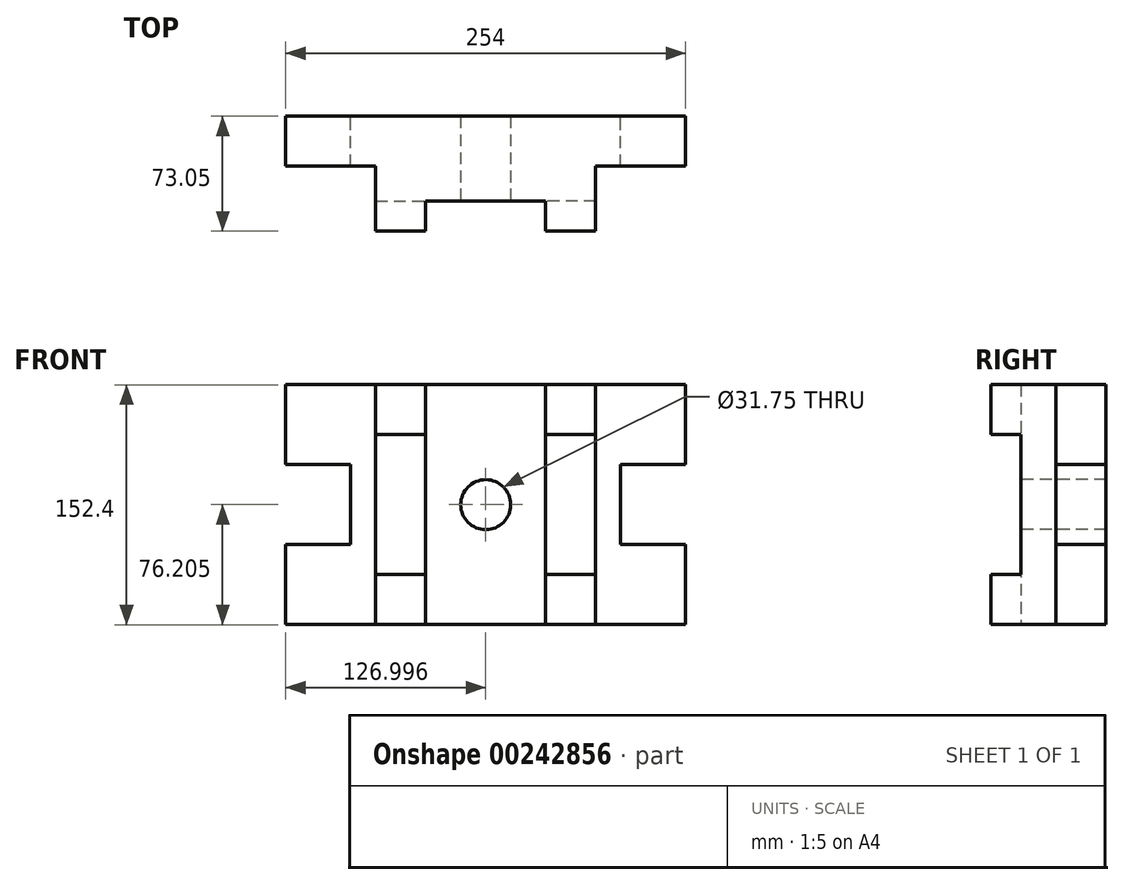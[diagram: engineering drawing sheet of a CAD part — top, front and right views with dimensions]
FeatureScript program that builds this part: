
annotation { "Feature Type Name" : "Feature", "Feature Type Description" : "" }
export const myFeature = defineFeature(function(context is Context, id is Id, definition is map)
    precondition{}
    {
        {
            var Q0;
            Q0=qCreatedBy(makeId("Front.planeOp"),FACE);
            var sketch = newSketch(context, id + "F0", { "sketchPlane" : qUnion([Q0])});
            skLineSegment(sketch, "E0.bottom", {"start": v(-138.15, 69.94) * mm, "end": v(115.85, 69.94) * mm});
            skLineSegment(sketch, "E0.top", {"start": v(-138.15, -82.46) * mm, "end": v(115.85, -82.46) * mm});
            skLineSegment(sketch, "E0.left", {"start": v(-138.15, 69.94) * mm, "end": v(-138.15, 19.14) * mm});
            skLineSegment(sketch, "E0.right", {"start": v(115.85, 69.94) * mm, "end": v(115.85, 19.14) * mm});
            skPoint(sketch, "E1", {"position": v(-138.15, 19.14) * mm});
            skPoint(sketch, "E2", {"position": v(-138.15, -31.66) * mm});
            skLineSegment(sketch, "E3.0", {"start": v(-96.88, 19.14) * mm, "end": v(-96.88, -31.66) * mm});
            skLineSegment(sketch, "E4", {"start": v(-138.15, 19.14) * mm, "end": v(-96.88, 19.14) * mm});
            skLineSegment(sketch, "E5", {"start": v(-138.15, -31.66) * mm, "end": v(-96.88, -31.66) * mm});
            skPoint(sketch, "E6", {"position": v(115.85, 19.14) * mm});
            skPoint(sketch, "E7", {"position": v(115.85, -31.66) * mm});
            skLineSegment(sketch, "E8.0", {"start": v(74.57, 19.14) * mm, "end": v(74.57, -31.66) * mm});
            skLineSegment(sketch, "E9", {"start": v(115.85, 19.14) * mm, "end": v(74.57, 19.14) * mm});
            skLineSegment(sketch, "E10", {"start": v(74.57, -31.66) * mm, "end": v(115.85, -31.66) * mm});
            skLineSegment(sketch, "E11.trimOffspring", {"start": v(-138.15, -31.66) * mm, "end": v(-138.15, -82.46) * mm});
            skLineSegment(sketch, "E12.trimOffspring", {"start": v(115.85, -31.66) * mm, "end": v(115.85, -82.46) * mm});
            skSolve(sketch);
        }
        {
            var Q0;
            Q0 = qSketchRegion(id + "F0", true);
            extrude(context, id + "F1", {"entities" : qUnion([Q0]), "depth" : 31.75 * mm});
        }
        {
            var Q0;
            Q0=makeQuery(id+"F1.opExtrude","CAP_FACE",FACE,{"disambiguationData":[OSD([sQuery(id+"F0.wireOp",EDGE,"E0.bottom"),sQuery(id+"F0.wireOp",EDGE,"E0.top"),sQuery(id+"F0.wireOp",EDGE,"E0.left"),sQuery(id+"F0.wireOp",EDGE,"E0.right"),sQuery(id+"F0.wireOp",EDGE,"E3.0"),sQuery(id+"F0.wireOp",EDGE,"E4"),sQuery(id+"F0.wireOp",EDGE,"E5"),sQuery(id+"F0.wireOp",EDGE,"E8.0"),sQuery(id+"F0.wireOp",EDGE,"E9"),sQuery(id+"F0.wireOp",EDGE,"E10"),sQuery(id+"F0.wireOp",EDGE,"E11.trimOffspring"),sQuery(id+"F0.wireOp",EDGE,"E12.trimOffspring")])],"isStart":false});
            var sketch = newSketch(context, id + "F2", { "sketchPlane" : qUnion([Q0])});
            skLineSegment(sketch, "E13", {"start": v(-81, 69.94) * mm, "end": v(-81, -82.46) * mm});
            skLineSegment(sketch, "E14", {"start": v(58.7, 69.94) * mm, "end": v(58.7, -82.46) * mm});
            skSolve(sketch);
        }
        {
            var Q0;
            {var subQ0=sQuery(id+"F2.wireOp",EDGE,"E13");Q0=makeQuery(id+"F2.imprint","IMPRINT",FACE,{"disambiguationData":[TD([[makeQuery(id+"F2.imprint","IMPRINT",EDGE,{"derivedFrom":subQ0}),1.0]])]});}
            extrude(context, id + "F3", {"entities" : qUnion([Q0]), "operationType" : NewBodyOperationType.ADD, "depth" : 22.22 * mm});
        }
        {
            var Q0;
            Q0=makeQuery(id+"F3.opExtrude","CAP_FACE",FACE,{"disambiguationData":[OSD([sQuery(id+"F0.wireOp",EDGE,"E0.bottom"),sQuery(id+"F0.wireOp",EDGE,"E0.top"),sQuery(id+"F2.wireOp",EDGE,"E13"),sQuery(id+"F2.wireOp",EDGE,"E14")])],"isStart":false});
            var sketch = newSketch(context, id + "F4", { "sketchPlane" : qUnion([Q0])});
            skLineSegment(sketch, "E15", {"start": v(-49.25, 69.94) * mm, "end": v(-49.25, -82.46) * mm});
            skLineSegment(sketch, "E16", {"start": v(26.95, 69.94) * mm, "end": v(26.95, -82.46) * mm});
            skSolve(sketch);
        }
        {
            var Q0;
            {var subQ0=sQuery(id+"F4.wireOp",EDGE,"E15");Q0=makeQuery(id+"F4.imprint","IMPRINT",FACE,{"disambiguationData":[TD([[makeQuery(id+"F4.imprint","IMPRINT",EDGE,{"derivedFrom":subQ0}),-1.0]])]});}
            var Q1;
            {var subQ0=sQuery(id+"F4.wireOp",EDGE,"E16");Q1=makeQuery(id+"F4.imprint","IMPRINT",FACE,{"disambiguationData":[TD([[makeQuery(id+"F4.imprint","IMPRINT",EDGE,{"derivedFrom":subQ0}),1.0]])]});}
            extrude(context, id + "F5", {"entities" : qUnion([Q0, Q1]), "operationType" : NewBodyOperationType.ADD, "depth" : 3 / 101.6 * mm});
        }
        {
            var Q0;
            Q0=makeQuery(id+"F5.opExtrude","CAP_FACE",FACE,{"disambiguationData":[OSD([sQuery(id+"F0.wireOp",EDGE,"E0.bottom"),sQuery(id+"F0.wireOp",EDGE,"E0.top"),sQuery(id+"F2.wireOp",EDGE,"E13"),sQuery(id+"F4.wireOp",EDGE,"E15")])],"isStart":false});
            var sketch = newSketch(context, id + "F6", { "sketchPlane" : qUnion([Q0])});
            skLineSegment(sketch, "E17", {"start": v(-81, 38.2) * mm, "end": v(-49.25, 38.2) * mm});
            skLineSegment(sketch, "E18", {"start": v(-81, -50.7) * mm, "end": v(-49.25, -50.7) * mm});
            skSolve(sketch);
        }
        {
            var Q0;
            Q0=makeQuery(id+"F5.opExtrude","CAP_FACE",FACE,{"disambiguationData":[OSD([sQuery(id+"F0.wireOp",EDGE,"E0.bottom"),sQuery(id+"F0.wireOp",EDGE,"E0.top"),sQuery(id+"F2.wireOp",EDGE,"E14"),sQuery(id+"F4.wireOp",EDGE,"E16")])],"isStart":false});
            var sketch = newSketch(context, id + "F7", { "sketchPlane" : qUnion([Q0])});
            skLineSegment(sketch, "E19", {"start": v(26.95, 38.2) * mm, "end": v(58.7, 38.2) * mm});
            skLineSegment(sketch, "E20", {"start": v(58.7, -50.7) * mm, "end": v(26.95, -50.7) * mm});
            skSolve(sketch);
        }
        {
            var Q0;
            {var subQ0=sQuery(id+"F7.wireOp",EDGE,"E19");Q0=makeQuery(id+"F7.imprint","IMPRINT",FACE,{"disambiguationData":[TD([[makeQuery(id+"F7.imprint","IMPRINT",EDGE,{"derivedFrom":subQ0}),1.0]])]});}
            var Q1;
            {var subQ0=sQuery(id+"F7.wireOp",EDGE,"E20");Q1=makeQuery(id+"F7.imprint","IMPRINT",FACE,{"disambiguationData":[TD([[makeQuery(id+"F7.imprint","IMPRINT",EDGE,{"derivedFrom":subQ0}),1.0]])]});}
            extrude(context, id + "F8", {"entities" : qUnion([Q0, Q1]), "operationType" : NewBodyOperationType.ADD, "depth" : 19.05 * mm});
        }
        {
            var Q0;
            {var subQ0=sQuery(id+"F6.wireOp",EDGE,"E17");Q0=makeQuery(id+"F6.imprint","IMPRINT",FACE,{"disambiguationData":[TD([[makeQuery(id+"F6.imprint","IMPRINT",EDGE,{"derivedFrom":subQ0}),1.0]])]});}
            var Q1;
            {var subQ0=sQuery(id+"F6.wireOp",EDGE,"E18");Q1=makeQuery(id+"F6.imprint","IMPRINT",FACE,{"disambiguationData":[TD([[makeQuery(id+"F6.imprint","IMPRINT",EDGE,{"derivedFrom":subQ0}),-1.0]])]});}
            extrude(context, id + "F9", {"entities" : qUnion([Q0, Q1]), "operationType" : NewBodyOperationType.ADD, "depth" : 19.05 * mm});
        }
        {
            var Q0;
            Q0=makeQuery(id+"F3.opExtrude","CAP_FACE",FACE,{"disambiguationData":[OSD([sQuery(id+"F0.wireOp",EDGE,"E0.bottom"),sQuery(id+"F0.wireOp",EDGE,"E0.top"),sQuery(id+"F2.wireOp",EDGE,"E13"),sQuery(id+"F2.wireOp",EDGE,"E14")])],"isStart":false});
            var sketch = newSketch(context, id + "F10", { "sketchPlane" : qUnion([Q0])});
            skCircle(sketch, "E21", {"center": v(-11.15, -6.26) * mm, "radius": 15.88 * mm});
            skSolve(sketch);
        }
        {
            var Q0;
            Q0=makeQuery(id+"F10.imprint","IMPRINT",FACE,{"disambiguationData":[TD([[makeQuery(id+"F10.imprint","IMPRINT",EDGE,{"derivedFrom":sQuery(id+"F10.wireOp",EDGE,"E21")}),1.0]])]});
            extrude(context, id + "F11", {"entities" : qUnion([Q0]), "operationType" : NewBodyOperationType.REMOVE, "endBound" : BoundingType.THROUGH_ALL, "oppositeDirection" : true, "depth" : 53.97 * mm});
        }
    });
